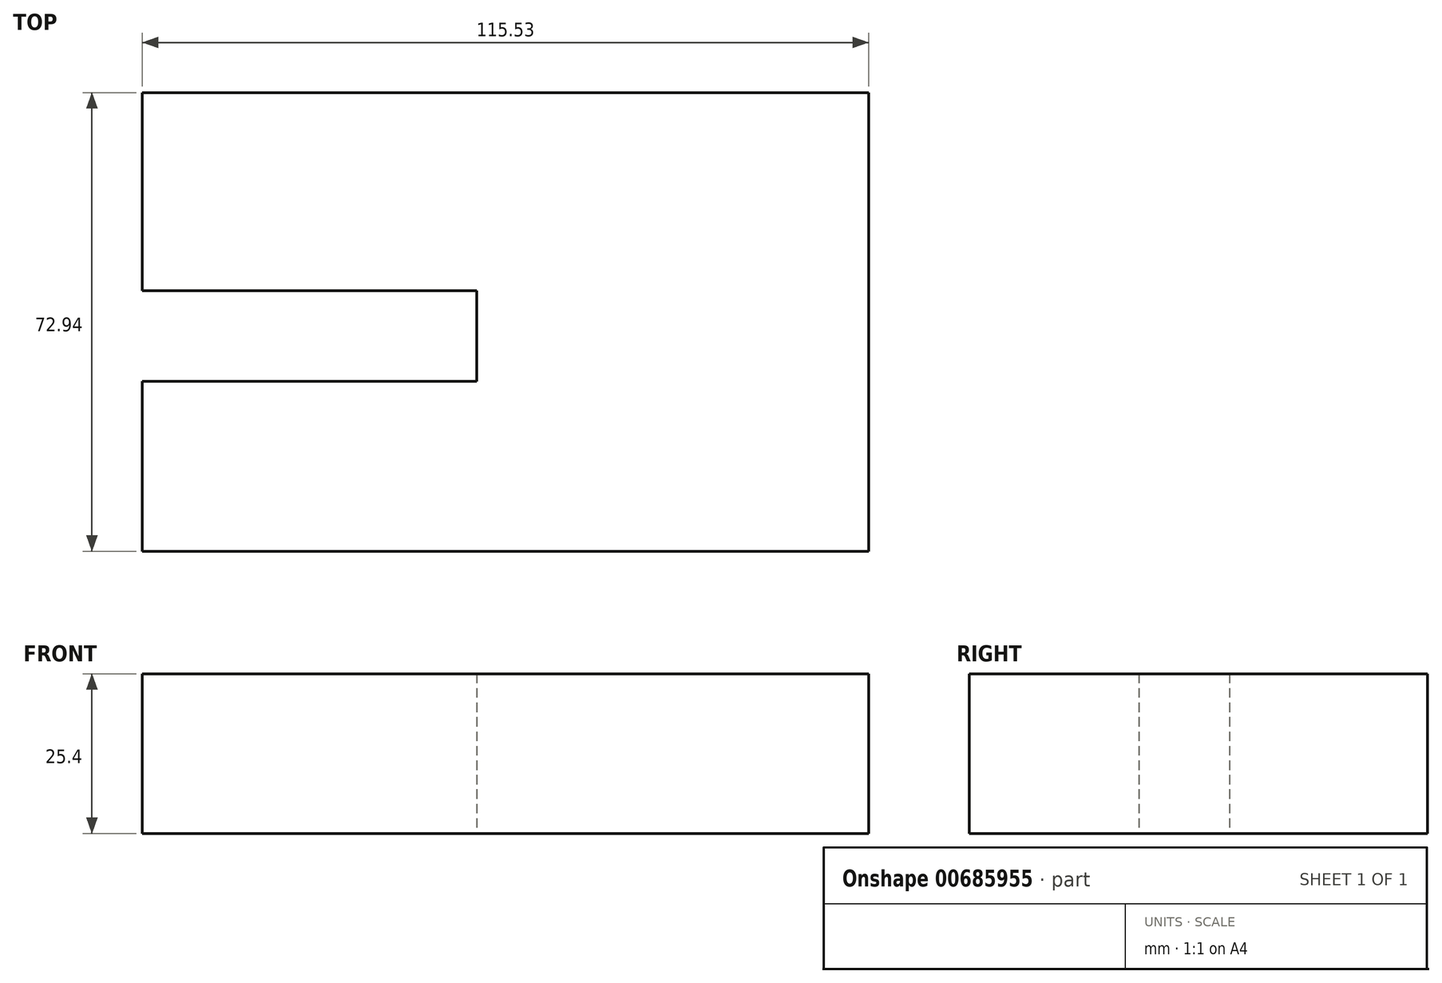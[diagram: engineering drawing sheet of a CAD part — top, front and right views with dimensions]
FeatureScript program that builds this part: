
annotation { "Feature Type Name" : "Feature", "Feature Type Description" : "" }
export const myFeature = defineFeature(function(context is Context, id is Id, definition is map)
    precondition{}
    {
        {
            var Q0;
            Q0=qCreatedBy(makeId("Top.planeOp"),FACE);
            var sketch = newSketch(context, id + "F0", { "sketchPlane" : qUnion([Q0])});
            skLineSegment(sketch, "E0.bottom", {"start": v(-53.18, 45.73) * mm, "end": v(62.35, 45.73) * mm});
            skLineSegment(sketch, "E0.top", {"start": v(-53.18, 45.92) * mm, "end": v(62.35, 45.92) * mm});
            skLineSegment(sketch, "E0.left", {"start": v(-53.18, 45.73) * mm, "end": v(-53.18, 45.92) * mm});
            skLineSegment(sketch, "E0.right", {"start": v(62.35, 45.73) * mm, "end": v(62.35, 45.92) * mm});
            skLineSegment(sketch, "E1.bottom", {"start": v(62.35, 45.73) * mm, "end": v(62.35, 45.73) * mm});
            skLineSegment(sketch, "E1.top", {"start": v(62.35, -28.55) * mm, "end": v(62.35, -28.55) * mm});
            skLineSegment(sketch, "E1.left", {"start": v(62.35, 45.73) * mm, "end": v(62.35, -28.55) * mm});
            skLineSegment(sketch, "E1.right", {"start": v(62.35, 45.73) * mm, "end": v(62.35, -28.55) * mm});
            skLineSegment(sketch, "E2.bottom", {"start": v(-53.18, 45.92) * mm, "end": v(-53.18, 45.92) * mm});
            skLineSegment(sketch, "E2.top", {"start": v(-53.18, 14.42) * mm, "end": v(-53.18, 14.42) * mm});
            skLineSegment(sketch, "E2.left", {"start": v(-53.18, 45.92) * mm, "end": v(-53.18, 14.42) * mm});
            skLineSegment(sketch, "E2.right", {"start": v(-53.18, 45.92) * mm, "end": v(-53.18, 14.42) * mm});
            skLineSegment(sketch, "E3.bottom", {"start": v(-53.18, 14.42) * mm, "end": v(0, 14.42) * mm});
            skLineSegment(sketch, "E3.top", {"start": v(-53.18, 14.42) * mm, "end": v(0, 14.42) * mm});
            skLineSegment(sketch, "E3.right", {"start": v(0, 14.42) * mm, "end": v(0, 14.42) * mm});
            skLineSegment(sketch, "E4.top", {"start": v(0, 0) * mm, "end": v(0, 0) * mm});
            skLineSegment(sketch, "E4.left", {"start": v(0, 14.42) * mm, "end": v(0, 0) * mm});
            skLineSegment(sketch, "E4.right", {"start": v(0, 14.42) * mm, "end": v(0, 0) * mm});
            skLineSegment(sketch, "E5.bottom", {"start": v(0, 0) * mm, "end": v(-53.18, 0) * mm});
            skLineSegment(sketch, "E5.top", {"start": v(0, 0) * mm, "end": v(-53.18, 0) * mm});
            skLineSegment(sketch, "E5.right", {"start": v(-53.18, 0) * mm, "end": v(-53.18, 0) * mm});
            skLineSegment(sketch, "E6.top", {"start": v(-53.18, -27.02) * mm, "end": v(-53.18, -27.02) * mm});
            skLineSegment(sketch, "E6.left", {"start": v(-53.18, 0) * mm, "end": v(-53.18, -27.02) * mm});
            skLineSegment(sketch, "E6.right", {"start": v(-53.18, 0) * mm, "end": v(-53.18, -27.02) * mm});
            skLineSegment(sketch, "E7.bottom", {"start": v(-53.18, -27.02) * mm, "end": v(63.87, -27.02) * mm});
            skLineSegment(sketch, "E7.top", {"start": v(-53.18, -27.02) * mm, "end": v(63.87, -27.02) * mm});
            skLineSegment(sketch, "E7.right", {"start": v(63.87, -27.02) * mm, "end": v(63.87, -27.02) * mm});
            skSolve(sketch);
        }
        {
            var Q0;
            Q0 = qSketchRegion(id + "F0", true);
            extrude(context, id + "F1", {"entities" : qUnion([Q0]), "depth" : 25.4 * mm, "offsetDistance" : 25.4 * mm});
        }
    });
